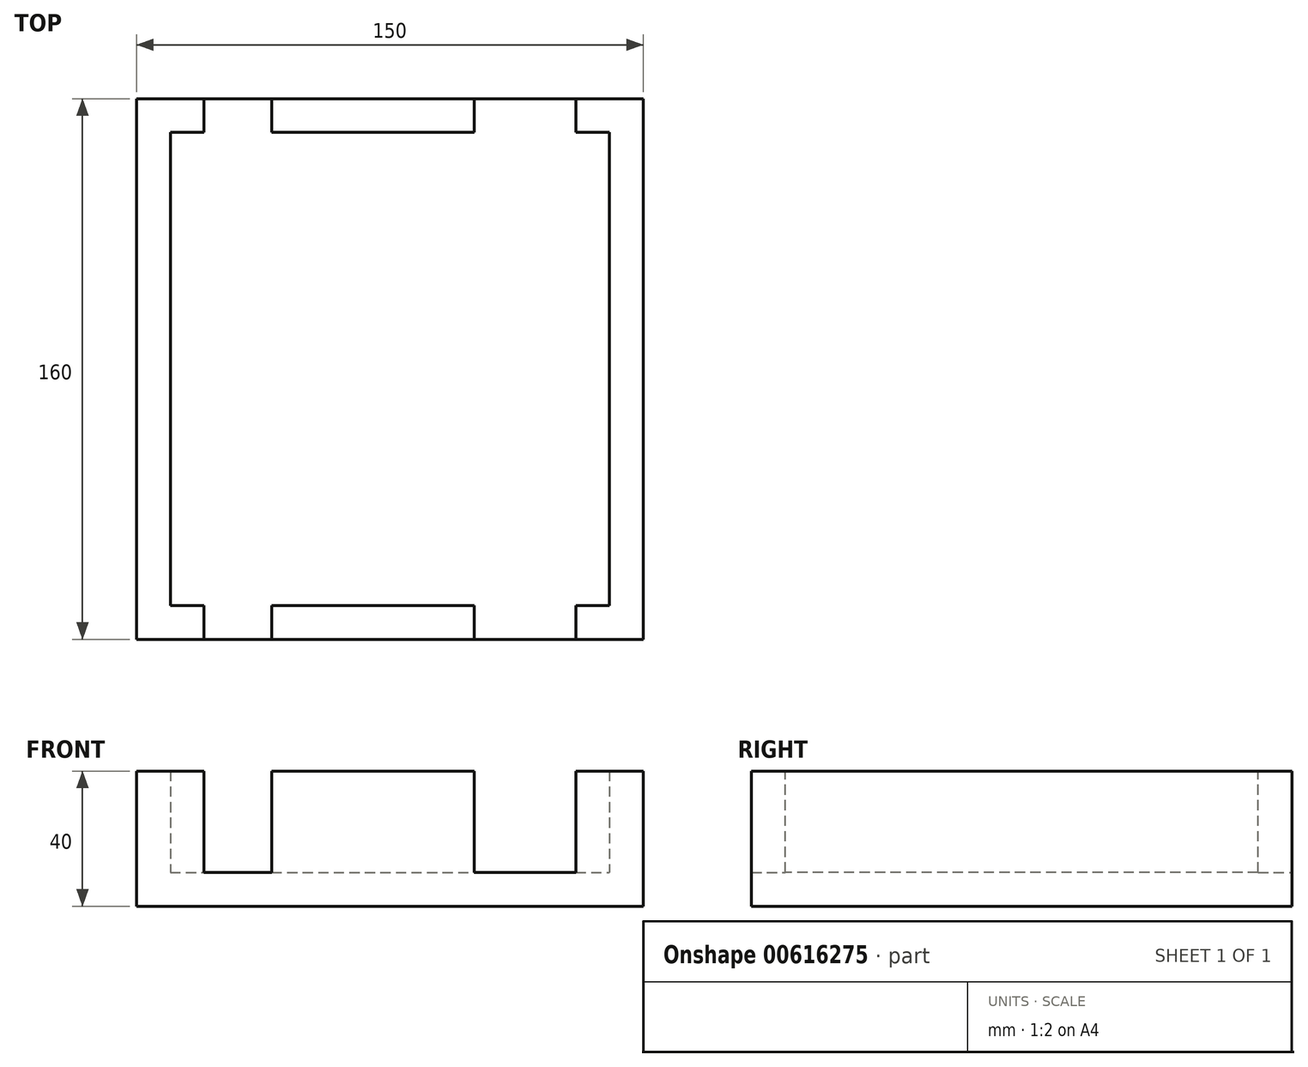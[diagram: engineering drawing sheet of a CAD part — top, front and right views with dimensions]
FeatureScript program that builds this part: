
annotation { "Feature Type Name" : "Feature", "Feature Type Description" : "" }
export const myFeature = defineFeature(function(context is Context, id is Id, definition is map)
    precondition{}
    {
        {
            var Q0;
            Q0=qCreatedBy(makeId("Top.planeOp"),FACE);
            var sketch = newSketch(context, id + "F0", { "sketchPlane" : qUnion([Q0])});
            skLineSegment(sketch, "E0.bottom", {"start": v(-75, 80) * mm, "end": v(75, 80) * mm});
            skLineSegment(sketch, "E0.top", {"start": v(-75, -80) * mm, "end": v(75, -80) * mm});
            skLineSegment(sketch, "E0.left", {"start": v(-75, 80) * mm, "end": v(-75, -80) * mm});
            skLineSegment(sketch, "E0.right", {"start": v(75, 80) * mm, "end": v(75, -80) * mm});
            skPoint(sketch, "E0.middle", {"position": v(0, 0) * mm});
            skSolve(sketch);
        }
        {
            var Q0;
            Q0=makeQuery(id+"F0.imprint","IMPRINT",FACE,{"disambiguationData":[TD([[makeQuery(id+"F0.imprint","IMPRINT",EDGE,{"derivedFrom":sQuery(id+"F0.wireOp",EDGE,"E0.bottom")}),-1.0]])]});
            extrude(context, id + "F1", {"entities" : qUnion([Q0]), "depth" : 10 * mm, "offsetDistance" : 25 * mm});
        }
        {
            var Q0;
            Q0=makeQuery(id+"F1.opExtrude","CAP_FACE",FACE,{"disambiguationData":[OSD([sQuery(id+"F0.wireOp",EDGE,"E0.bottom"),sQuery(id+"F0.wireOp",EDGE,"E0.top"),sQuery(id+"F0.wireOp",EDGE,"E0.left"),sQuery(id+"F0.wireOp",EDGE,"E0.right")])],"isStart":false});
            var sketch = newSketch(context, id + "F2", { "sketchPlane" : qUnion([Q0])});
            skLineSegment(sketch, "E1.bottom", {"start": v(-65, 70) * mm, "end": v(65, 70) * mm});
            skLineSegment(sketch, "E1.top", {"start": v(-65, -70) * mm, "end": v(65, -70) * mm});
            skLineSegment(sketch, "E1.left", {"start": v(-65, 70) * mm, "end": v(-65, -70) * mm});
            skLineSegment(sketch, "E1.right", {"start": v(65, 70) * mm, "end": v(65, -70) * mm});
            skPoint(sketch, "E1.middle", {"position": v(0, 0) * mm});
            skSolve(sketch);
        }
        {
            var Q0;
            Q0=makeQuery(id+"F2.imprint","IMPRINT",FACE,{"disambiguationData":[TD([[makeQuery(id+"F2.imprint","IMPRINT",EDGE,{"derivedFrom":sQuery(id+"F2.wireOp",EDGE,"E1.bottom")}),1.0]])]});
            extrude(context, id + "F3", {"entities" : qUnion([Q0]), "operationType" : NewBodyOperationType.ADD, "depth" : 30 * mm, "offsetDistance" : 25 * mm});
        }
        {
            var Q0;
            Q0=makeQuery(id+"F3.opExtrude","CAP_FACE",FACE,{"disambiguationData":[OSD([sQuery(id+"F0.wireOp",EDGE,"E0.bottom"),sQuery(id+"F0.wireOp",EDGE,"E0.top"),sQuery(id+"F0.wireOp",EDGE,"E0.left"),sQuery(id+"F0.wireOp",EDGE,"E0.right"),sQuery(id+"F2.wireOp",EDGE,"E1.bottom"),sQuery(id+"F2.wireOp",EDGE,"E1.top"),sQuery(id+"F2.wireOp",EDGE,"E1.left"),sQuery(id+"F2.wireOp",EDGE,"E1.right")])],"isStart":false});
            var sketch = newSketch(context, id + "F4", { "sketchPlane" : qUnion([Q0])});
            skLineSegment(sketch, "E2.bottom", {"start": v(-35, 70) * mm, "end": v(-55, 70) * mm});
            skLineSegment(sketch, "E2.top", {"start": v(-35, 80) * mm, "end": v(-55, 80) * mm});
            skLineSegment(sketch, "E2.left", {"start": v(-35, 70) * mm, "end": v(-35, 80) * mm});
            skLineSegment(sketch, "E2.right", {"start": v(-55, 70) * mm, "end": v(-55, 80) * mm});
            skPoint(sketch, "E2.middle", {"position": v(-45, 75) * mm});
            skSolve(sketch);
        }
        {
            var Q0;
            Q0=makeQuery(id+"F4.imprint","IMPRINT",FACE,{"disambiguationData":[TD([[makeQuery(id+"F4.imprint","IMPRINT",EDGE,{"derivedFrom":sQuery(id+"F4.wireOp",EDGE,"E2.bottom")}),1.0]])]});
            extrude(context, id + "F5", {"entities" : qUnion([Q0]), "operationType" : NewBodyOperationType.REMOVE, "oppositeDirection" : true, "depth" : 30 * mm, "offsetDistance" : 25 * mm});
        }
        {
            var Q0;
            Q0=makeQuery(id+"F3.opExtrude","CAP_FACE",FACE,{"disambiguationData":[OSD([sQuery(id+"F0.wireOp",EDGE,"E0.bottom"),sQuery(id+"F0.wireOp",EDGE,"E0.top"),sQuery(id+"F0.wireOp",EDGE,"E0.left"),sQuery(id+"F0.wireOp",EDGE,"E0.right"),sQuery(id+"F2.wireOp",EDGE,"E1.bottom"),sQuery(id+"F2.wireOp",EDGE,"E1.top"),sQuery(id+"F2.wireOp",EDGE,"E1.left"),sQuery(id+"F2.wireOp",EDGE,"E1.right")])],"isStart":false});
            var sketch = newSketch(context, id + "F6", { "sketchPlane" : qUnion([Q0])});
            skLineSegment(sketch, "E3.bottom", {"start": v(55, 70) * mm, "end": v(25, 70) * mm});
            skLineSegment(sketch, "E3.top", {"start": v(55, 80) * mm, "end": v(25, 80) * mm});
            skLineSegment(sketch, "E3.left", {"start": v(55, 70) * mm, "end": v(55, 80) * mm});
            skLineSegment(sketch, "E3.right", {"start": v(25, 70) * mm, "end": v(25, 80) * mm});
            skPoint(sketch, "E3.middle", {"position": v(40, 75) * mm});
            skSolve(sketch);
        }
        {
            var Q0;
            Q0=makeQuery(id+"F6.imprint","IMPRINT",FACE,{"disambiguationData":[TD([[makeQuery(id+"F6.imprint","IMPRINT",EDGE,{"derivedFrom":sQuery(id+"F6.wireOp",EDGE,"E3.bottom")}),1.0]])]});
            extrude(context, id + "F7", {"entities" : qUnion([Q0]), "operationType" : NewBodyOperationType.REMOVE, "oppositeDirection" : true, "depth" : 30 * mm, "offsetDistance" : 25 * mm});
        }
        {
            var Q0;
            {var subQ0=sQuery(id+"F0.wireOp",EDGE,"E0.top");var subQ1=sQuery(id+"F0.wireOp",EDGE,"E0.bottom");var subQ2=sQuery(id+"F2.wireOp",EDGE,"E1.right");var subQ3=sQuery(id+"F2.wireOp",EDGE,"E1.bottom");var subQ4=sQuery(id+"F0.wireOp",EDGE,"E0.left");var subQ5=sQuery(id+"F2.wireOp",EDGE,"E1.left");var subQ6=sQuery(id+"F0.wireOp",EDGE,"E0.right");var subQ7=sQuery(id+"F2.wireOp",EDGE,"E1.top");Q0=makeQuery(id+"F7.boolean.opBoolean","SPLIT",FACE,{"disambiguationData":[TD([makeQuery(id+"F1.opExtrude","SWEPT_FACE",FACE,{"disambiguationData":[OSD([subQ0])]})])],"derivedFrom":makeQuery(id+"F3.opExtrude","CAP_FACE",FACE,{"disambiguationData":[OSD([subQ1,subQ0,subQ4,subQ6,subQ3,subQ7,subQ5,subQ2])],"isStart":false})});}
            var sketch = newSketch(context, id + "F8", { "sketchPlane" : qUnion([Q0])});
            skLineSegment(sketch, "E4.bottom", {"start": v(-35, -80) * mm, "end": v(-55, -80) * mm});
            skLineSegment(sketch, "E4.top", {"start": v(-35, -70) * mm, "end": v(-55, -70) * mm});
            skLineSegment(sketch, "E4.left", {"start": v(-35, -80) * mm, "end": v(-35, -70) * mm});
            skLineSegment(sketch, "E4.right", {"start": v(-55, -80) * mm, "end": v(-55, -70) * mm});
            skPoint(sketch, "E4.middle", {"position": v(-45, -75) * mm});
            skSolve(sketch);
        }
        {
            var Q0;
            Q0=makeQuery(id+"F8.imprint","IMPRINT",FACE,{"disambiguationData":[TD([[makeQuery(id+"F8.imprint","IMPRINT",EDGE,{"derivedFrom":sQuery(id+"F8.wireOp",EDGE,"E4.bottom")}),1.0]])]});
            extrude(context, id + "F9", {"entities" : qUnion([Q0]), "operationType" : NewBodyOperationType.REMOVE, "oppositeDirection" : true, "depth" : 30 * mm, "offsetDistance" : 25 * mm});
        }
        {
            var Q0;
            {var subQ0=sQuery(id+"F0.wireOp",EDGE,"E0.right");var subQ2=sQuery(id+"F0.wireOp",EDGE,"E0.top");var subQ4=sQuery(id+"F0.wireOp",EDGE,"E0.bottom");var subQ6=sQuery(id+"F2.wireOp",EDGE,"E1.right");var subQ8=sQuery(id+"F2.wireOp",EDGE,"E1.top");var subQ12=makeQuery(id+"F1.opExtrude","SWEPT_FACE",FACE,{"disambiguationData":[OSD([subQ0])]});var subQ13=makeQuery(id+"F1.opExtrude","SWEPT_FACE",FACE,{"disambiguationData":[OSD([subQ2])]});var subQ14=sQuery(id+"F2.wireOp",EDGE,"E1.bottom");var subQ16=sQuery(id+"F0.wireOp",EDGE,"E0.left");var subQ17=sQuery(id+"F2.wireOp",EDGE,"E1.left");Q0=makeQuery(id+"F9.boolean.opBoolean","SPLIT",FACE,{"disambiguationData":[TD([subQ12])],"derivedFrom":makeQuery(id+"F7.boolean.opBoolean","SPLIT",FACE,{"disambiguationData":[TD([subQ13])],"derivedFrom":makeQuery(id+"F3.opExtrude","CAP_FACE",FACE,{"disambiguationData":[OSD([subQ4,subQ2,subQ16,subQ0,subQ14,subQ8,subQ17,subQ6])],"isStart":false})})});}
            var sketch = newSketch(context, id + "F10", { "sketchPlane" : qUnion([Q0])});
            skLineSegment(sketch, "E5.bottom", {"start": v(55, -80) * mm, "end": v(25, -80) * mm});
            skLineSegment(sketch, "E5.top", {"start": v(55, -70) * mm, "end": v(25, -70) * mm});
            skLineSegment(sketch, "E5.left", {"start": v(55, -80) * mm, "end": v(55, -70) * mm});
            skLineSegment(sketch, "E5.right", {"start": v(25, -80) * mm, "end": v(25, -70) * mm});
            skPoint(sketch, "E5.middle", {"position": v(40, -75) * mm});
            skSolve(sketch);
        }
        {
            var Q0;
            Q0=makeQuery(id+"F10.imprint","IMPRINT",FACE,{"disambiguationData":[TD([[makeQuery(id+"F10.imprint","IMPRINT",EDGE,{"derivedFrom":sQuery(id+"F10.wireOp",EDGE,"E5.bottom")}),1.0]])]});
            extrude(context, id + "F11", {"entities" : qUnion([Q0]), "operationType" : NewBodyOperationType.REMOVE, "oppositeDirection" : true, "depth" : 30 * mm, "offsetDistance" : 25 * mm});
        }
    });
